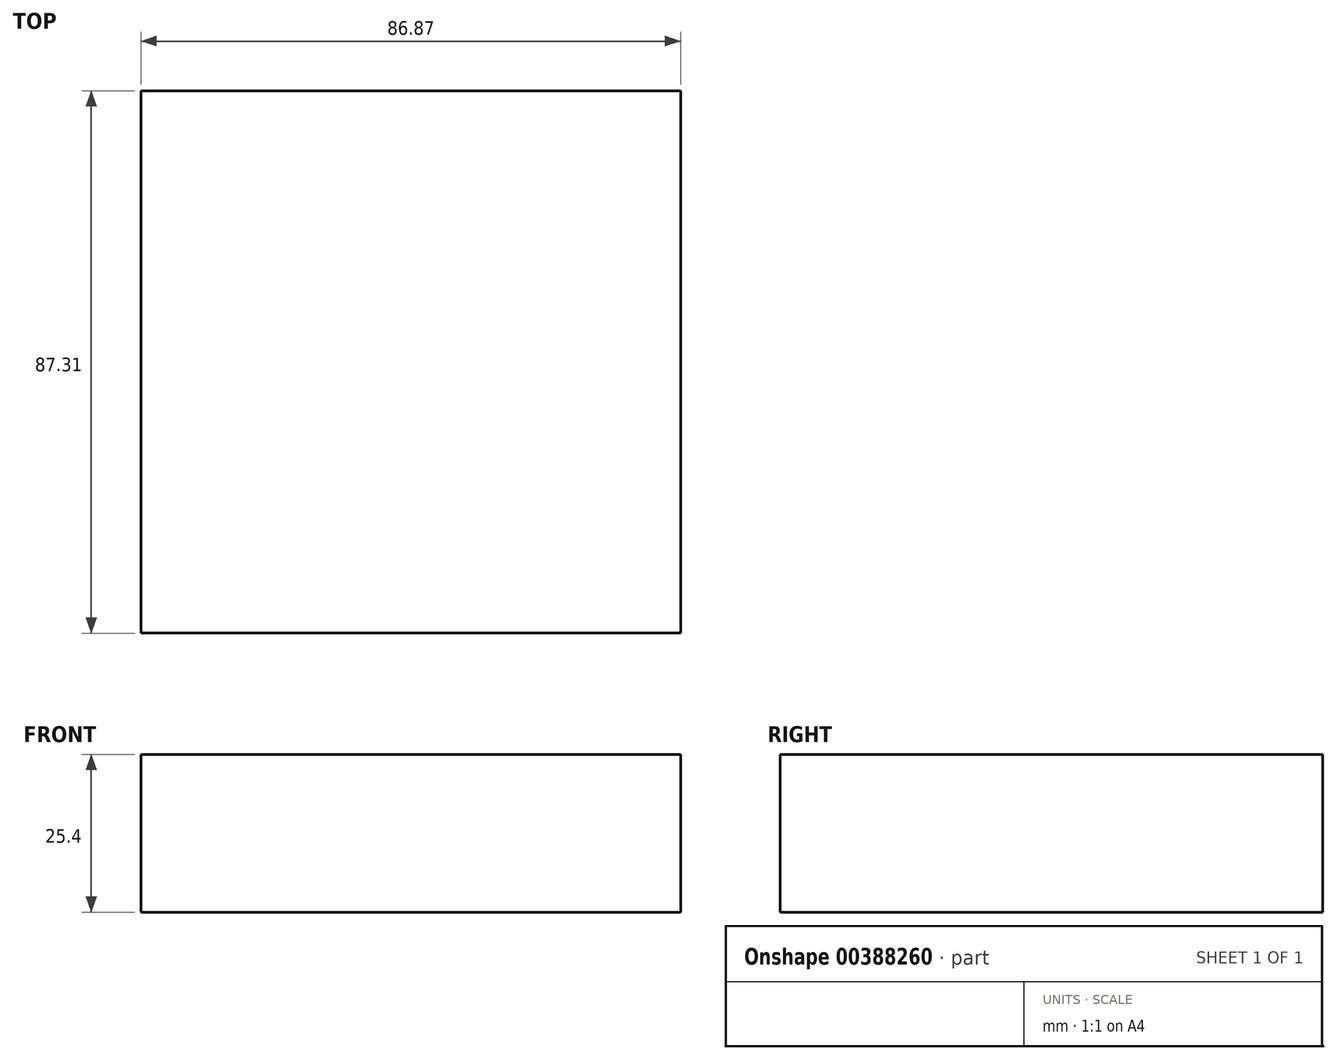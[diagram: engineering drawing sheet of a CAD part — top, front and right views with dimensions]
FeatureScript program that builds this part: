
annotation { "Feature Type Name" : "Feature", "Feature Type Description" : "" }
export const myFeature = defineFeature(function(context is Context, id is Id, definition is map)
    precondition{}
    {
        {
            var Q0;
            Q0=qCreatedBy(makeId("Top.planeOp"),FACE);
            var sketch = newSketch(context, id + "F0", { "sketchPlane" : qUnion([Q0])});
            skLineSegment(sketch, "E0.bottom", {"start": v(-38.26, 42.76) * mm, "end": v(48.6, 42.76) * mm});
            skLineSegment(sketch, "E0.top", {"start": v(-38.26, -44.55) * mm, "end": v(48.6, -44.55) * mm});
            skLineSegment(sketch, "E0.left", {"start": v(-38.26, 42.76) * mm, "end": v(-38.26, -44.55) * mm});
            skLineSegment(sketch, "E0.right", {"start": v(48.6, 42.76) * mm, "end": v(48.6, -44.55) * mm});
            skSolve(sketch);
        }
        {
            var Q0;
            Q0 = qSketchRegion(id + "F0", true);
            extrude(context, id + "F1", {"entities" : qUnion([Q0]), "depth" : 25.4 * mm});
        }
    });
